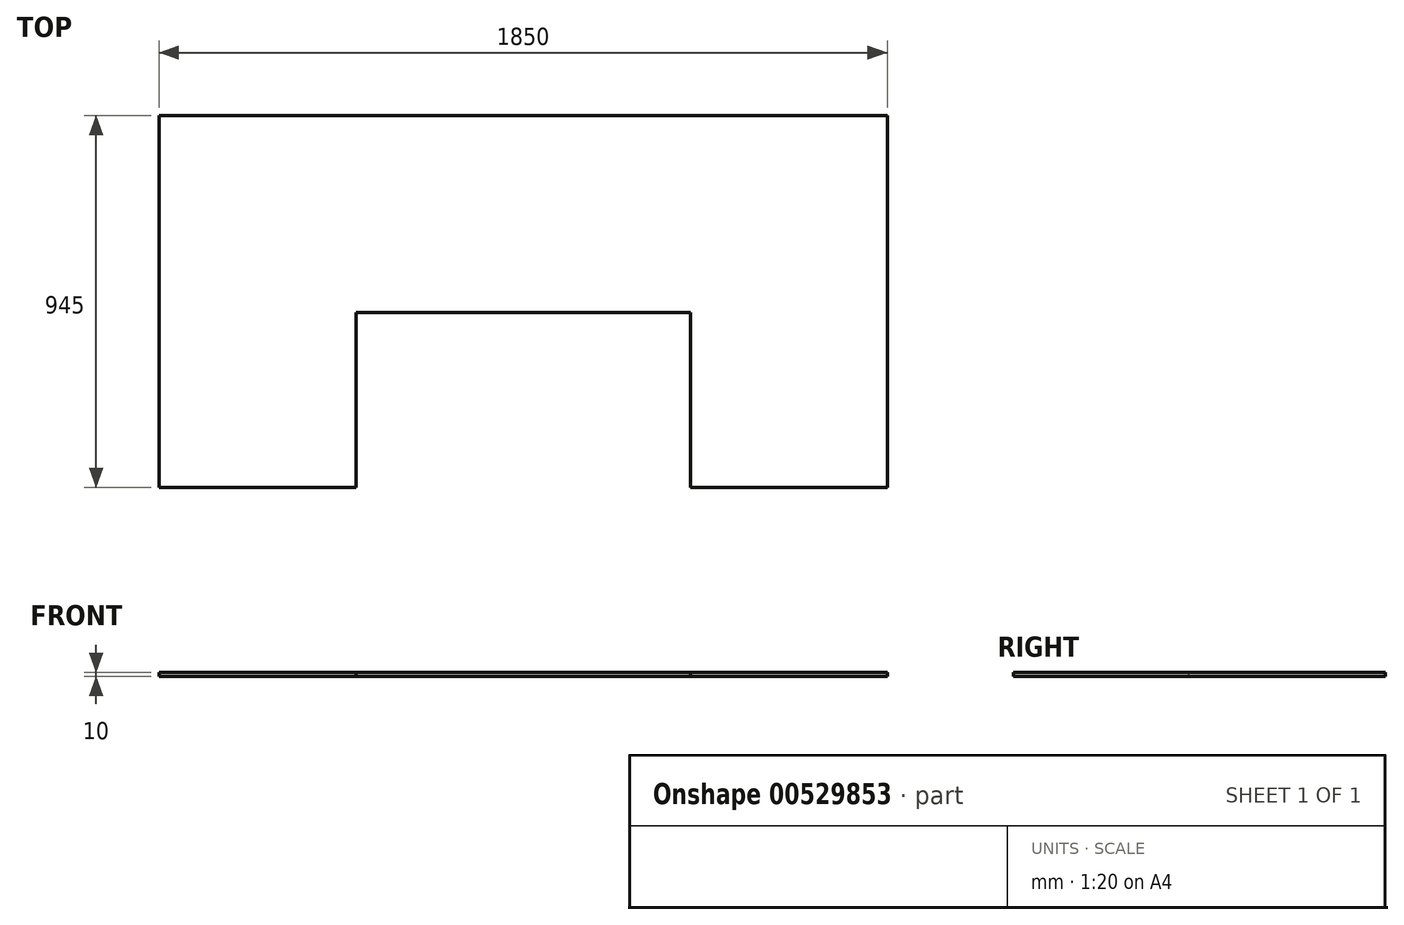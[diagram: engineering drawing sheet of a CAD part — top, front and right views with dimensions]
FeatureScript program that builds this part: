
annotation { "Feature Type Name" : "Feature", "Feature Type Description" : "" }
export const myFeature = defineFeature(function(context is Context, id is Id, definition is map)
    precondition{}
    {
        {
            var Q0;
            Q0=qCreatedBy(makeId("Top.planeOp"),FACE);
            var sketch = newSketch(context, id + "F0", { "sketchPlane" : qUnion([Q0])});
            skLineSegment(sketch, "E0", {"start": v(0, 0) * mm, "end": v(0, 945) * mm});
            skLineSegment(sketch, "E1", {"start": v(0, 945) * mm, "end": v(1850, 945) * mm});
            skLineSegment(sketch, "E2", {"start": v(1850, 945) * mm, "end": v(1850, 0) * mm});
            skLineSegment(sketch, "E3", {"start": v(1850, 0) * mm, "end": v(1350, 0) * mm});
            skLineSegment(sketch, "E4", {"start": v(1350, 0) * mm, "end": v(1350, 445) * mm});
            skLineSegment(sketch, "E5", {"start": v(1350, 445) * mm, "end": v(500, 445) * mm});
            skLineSegment(sketch, "E6", {"start": v(500, 445) * mm, "end": v(500, 0) * mm});
            skLineSegment(sketch, "E7", {"start": v(500, 0) * mm, "end": v(0, 0) * mm});
            skSolve(sketch);
        }
        {
            var Q0;
            Q0 = qSketchRegion(id + "F0", true);
            extrude(context, id + "F1", {"entities" : qUnion([Q0]), "depth" : 10 * mm, "offsetDistance" : 25 * mm});
        }
    });
